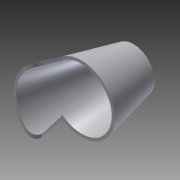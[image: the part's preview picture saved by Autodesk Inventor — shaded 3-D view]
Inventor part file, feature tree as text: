
AUTODESK INVENTOR PART (.ipt)
format: ipt  version: 2015 (Build 190159000, 159)  size: 169,472 bytes
history: native  units: mm
features: sketch x4, extrude x2, revolve x1, shell x1, hole x1, fillet x1, pattern_circular x1
ambient origin geometry x8: Origin, YZ Plane, XZ Plane, XY Plane, X Axis, Y Axis, Z Axis, Center Point
bodies: Body1 (feature_tree)
feature tree (11):
  revolve  "回転1"
  shell  "シェル2"  Thickness=22.5mm
  hole  "穴2"  [1 undecoded]
  extrude  "押し出し6"  Depth=85.0mm
  fillet  "フィレット3"  [1 undecoded]
  extrude  "押し出し7"  Depth=3.0mm
  pattern_circular  "円形状パターン2"  [2 undecoded]
  sketch  "スケッチ8"
  sketch  "スケッチ9"
  sketch  "スケッチ16"
  sketch  "スケッチ17"
note: 4 required parameter values undecoded (feature->parameter linkage not recoverable at this tier; creation-order binding heuristic only, values carry confidence <= 0.55)
